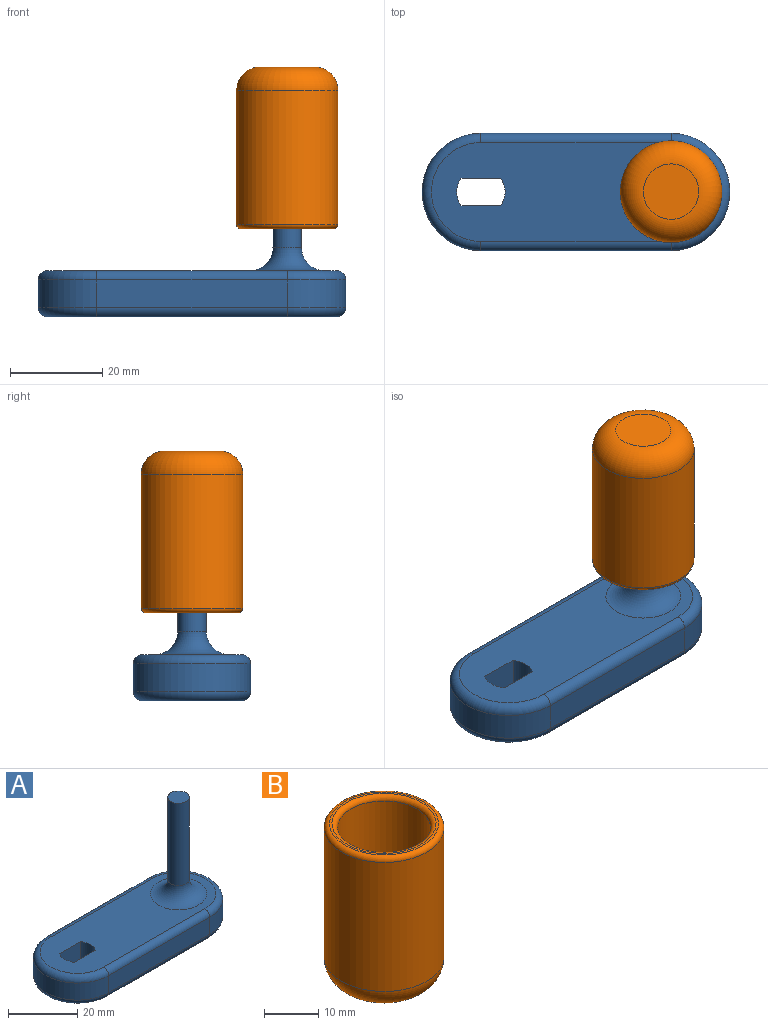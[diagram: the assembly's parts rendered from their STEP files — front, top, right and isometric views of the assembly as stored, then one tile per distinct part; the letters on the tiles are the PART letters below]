
ASSEMBLY  parts=2 mates=1
PART A: 21 faces, bbox 68.7x27.5x44 mm
  f0: plane 41.17x6mm, normal (0,1,0), area 247mm2, adj f1,f7,f16,f19
  f1: cylinder r=12.7mm len=25.4mm, axis (0,0,-1), area 239.4mm2, adj f0,f2,f14,f17
  f2: plane 41.17x6mm, normal (0,-1,0), area 247mm2, adj f1,f7,f13,f18
  f3: plane 10x8.62mm, normal (0,-1,0), area 86.2mm2, adj f4,f6,f8,f9
  f4: cylinder r=5.25mm len=10mm, axis (0,0,-1), area 63.9mm2, adj f3,f5,f8,f9
  f5: plane 10x8.62mm, normal (0,1,0), area 86.2mm2, adj f4,f6,f8,f9
  f6: cylinder r=5.25mm len=10mm, axis (0,0,-1), area 63.9mm2, adj f3,f5,f8,f9
  f7: cylinder r=12.7mm len=25.4mm, axis (0,0,-1), area 239.4mm2, adj f0,f2,f15,f20
  f8: plane 62.57x21.4mm, normal (0,0,1), area 975.2mm2, adj f3,f4,f5,f6,f12,f17,f18,f19
  f9: plane 62.57x21.4mm, normal (0,0,-1), area 1181.3mm2, adj f3,f4,f5,f6,f13,f14,f15,f16
  f10: cylinder r=3.1mm len=29mm, axis (0,0,-1), area 564.9mm2, adj f11,f12
  f11: plane 6.2x6.2mm, normal (0,0,1), area 30.2mm2, adj f10
  f12: torus R=8.1mm, axis (0,0,1), area 242.6mm2, adj f8,f10
  f13: cylinder r=2mm len=41.17mm, axis (1,0,0), area 129.3mm2, adj f2,f9,f14,f15
  f14: torus R=10.7mm, axis (0,0,1), area 118.2mm2, adj f1,f9,f13,f16
  f15: torus R=10.7mm, axis (0,0,1), area 118.2mm2, adj f7,f9,f13,f16
  f16: cylinder r=2mm len=41.17mm, axis (-1,0,0), area 129.3mm2, adj f0,f9,f14,f15
  f17: torus R=10.7mm, axis (0,0,1), area 118.2mm2, adj f1,f8,f18,f19
  f18: cylinder r=2mm len=41.17mm, axis (-1,0,0), area 129.3mm2, adj f2,f8,f17,f20
  f19: cylinder r=2mm len=41.17mm, axis (1,0,0), area 129.3mm2, adj f0,f8,f17,f20
  f20: torus R=10.7mm, axis (0,0,1), area 118.2mm2, adj f7,f8,f18,f19
PART B: 8 faces, bbox 23.8x23.8x35 mm
  f0: cylinder r=11mm len=29mm, axis (0,0,-1), area 2004.3mm2, adj f5,f7
  f1: plane 12x12mm, normal (0,0,-1), area 113.1mm2, adj f5
  f2: cylinder r=8.55mm len=31mm, axis (0,0,-1), area 1665.4mm2, adj f4,f6
  f3: plane 20x20mm, normal (0,0,1), area 27.6mm2, adj f6,f7
  f4: plane 17.1x17.1mm, normal (0,0,1), area 229.7mm2, adj f2
  f5: torus R=6mm, axis (0,0,1), area 453.2mm2, adj f0,f1
  f6: torus R=9.55mm, axis (0,0,1), area 88mm2, adj f2,f3
  f7: torus R=10mm, axis (0,0,1), area 105mm2, adj f0,f3
PLACE A t=(14.72,-12.7,12.9)mm
PLACE B rot(axis=(1,0,0),180deg) t=(69.74,39.87,66.97)mm
MATE slider B.f0 <-> A.f7  axis (0,0,-1) through (33.58,20.49,63.97)mm
